# Revit family: PRD_FrankeWS_DspnsrsAndAccptncUnts_STRATOSHygieneBagDispenser_STRX615
name_source: partatom
category: Specialty Equipment
revit_build: Autodesk Revit 2018 (Build: 20190510_1515(x64)
units: mm (PartAtom-declared; Revit-internal decimal feet)

## family parameters
Cut with Voids When Loaded = No
Host = Face
OmniClass Number = 23.40.20.21
OmniClass Title = Toilet and Bath Specialties
Part Type = Normal
Room Calculation Point = No
Round Connector Dimension = Use Diameter
Shared = No

## types (1)
- STRX615
    AssetType = Fixed
    BIMObjectName = PRD_AR_DispensersAndAcceptanceUnits_STRATOSHygieneBagDispenser_STRX615
    Category = Pr_40_70_22, Dispensers and acceptance units
    Default Elevation = 900 mm  [stored 2.95276 ft]
    Description = Hygiene bag dispenser for wall mounting, stainless steel, surface satin finished, with InoxPlus surface refinement for the reduction of finger marks and better cleaning characteristics (easy to clean), material thickness 1.2/1.5 mm, with inspection window, includes stainless steel screws and dowels.
    DispenserMaterial = PRD_AR_StainlessSteel_SatinFinished
    DurationUnit = year
    Features = stainless steel, surface satin finished
    FillingQuantity = 100
    FillingQuantityUom = Pieces
    Finish = satin finished
    GrossWeight = 1.67 kg
    IfcExportAs = IfcFurnitureType
    IfcExportType = USERDEFINED
    IntegralAccessories = incl. stainless steel screws and dowels
    IsBuiltIn = TRUE
    Lock = No lock
    MainColor = stainless steel
    Manufacturer = KWC Group AG
    ManufacturerName = KWC Group AG
    ManufacturerURL = www.kwc.com
    Material = stainless steel
    MaterialCode = 1.4301
    MaterialThickness = 1.50 mm
    Model = STRX615
    ModelNumber = 2000100014
    ModelReference = STRX615
    Name = Hygiene Bag Dispenser STRX615
    NetWeight = 1.44 kg
    NominalDepth = 90 mm  [stored 0.295276 ft]
    NominalHeight = 250 mm  [stored 0.82021 ft]
    NominalWidth = 156 mm  [stored 0.511811 ft]
    ProductInformation = https://pim.kwc.com
    Size = 156 x 250 x 90 mm
    Style = Hygiene bag dispenser
    SurfaceTreatment = InoxPlus (anti fingerprint)
    TypeOfConsumable = Hygiene bag
    TypeOfFixing = Screw
    TypeOfMounting = Wall mounting
    TypeOfOperation = Manual operation
    URL = www.kwc.com
    Uniclass2015Code = Pr_40_70_22
    Uniclass2015Title = Dispensers and acceptance units
    Uniclass2015Version = Products v1.10
    Version = 1
    WarrantyDurationUnit = year

note: [stored X ft] marks values corroborated as IEEE doubles in the binary element streams (Revit-internal decimal feet)

## geometry (parser evidence)
native form markers: Sweep x4
no freeform markers — native parametric forms only
